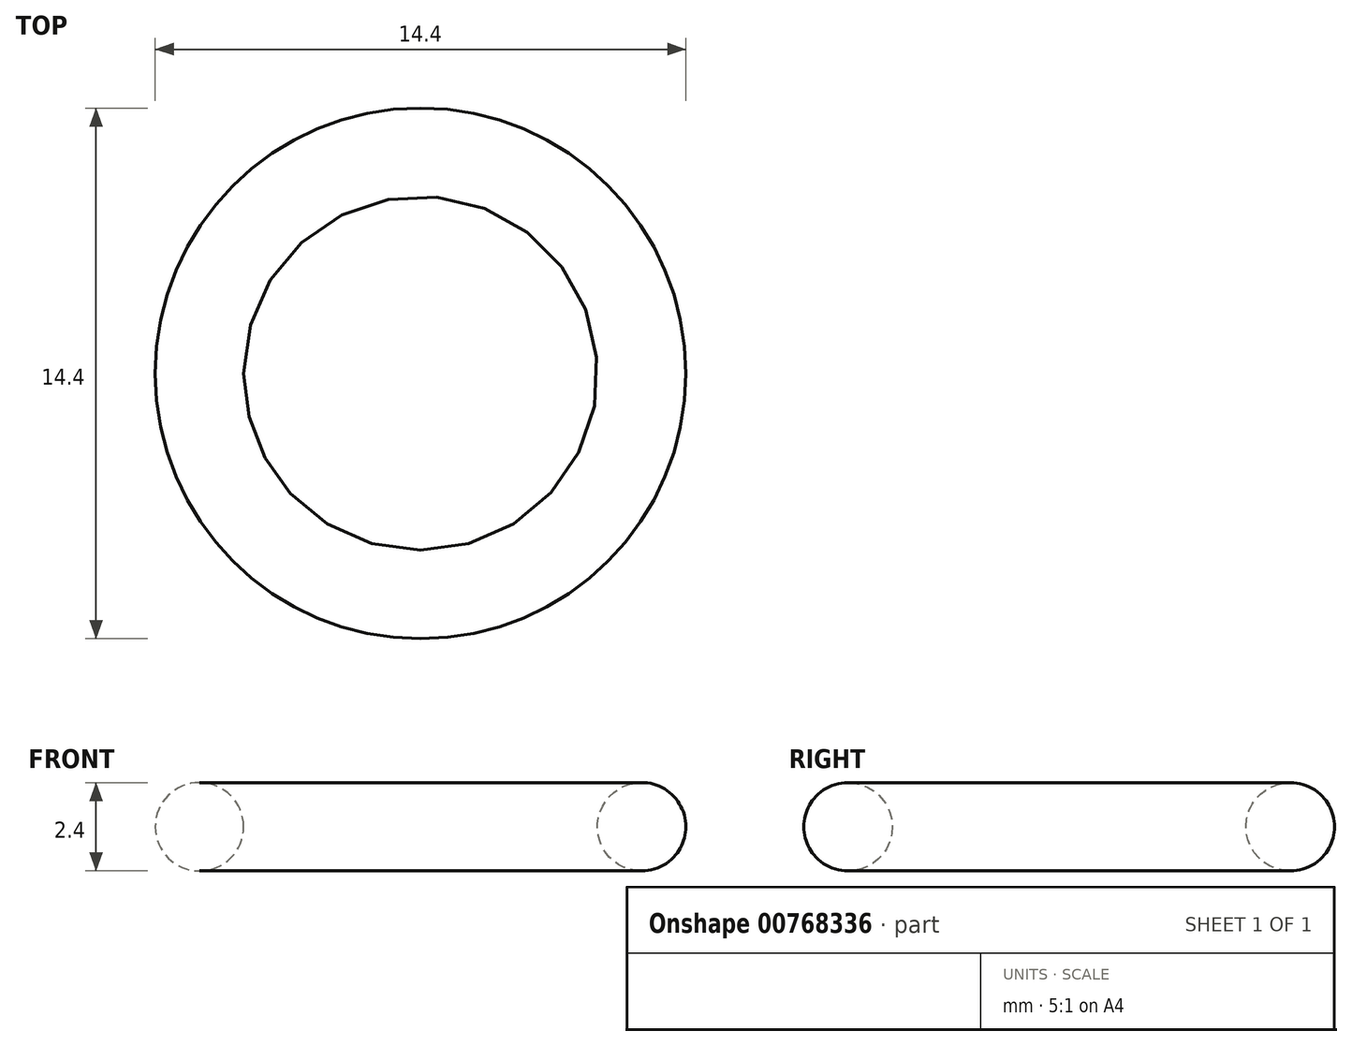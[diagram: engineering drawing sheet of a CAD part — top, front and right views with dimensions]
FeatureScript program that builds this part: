
annotation { "Feature Type Name" : "Feature", "Feature Type Description" : "" }
export const myFeature = defineFeature(function(context is Context, id is Id, definition is map)
    precondition{}
    {
        {
            var Q0;
            Q0=qCreatedBy(makeId("Front.planeOp"),FACE);
            var sketch = newSketch(context, id + "F0", { "sketchPlane" : qUnion([Q0])});
            skCircle(sketch, "E0", {"center": v(-6, 0) * mm, "radius": 1.2 * mm});
            skSolve(sketch);
        }
        {
            var Q0;
            Q0=qCreatedBy(makeId("Front.planeOp"),FACE);
            var sketch = newSketch(context, id + "F1", { "sketchPlane" : qUnion([Q0])});
            skLineSegment(sketch, "E1", {"start": v(0, -4.35) * mm, "end": v(0, 5.64) * mm});
            skSolve(sketch);
        }
        {
            var Q0;
            Q0=makeQuery(id+"F0.imprint","IMPRINT",FACE,{"disambiguationData":[TD([[makeQuery(id+"F0.imprint","IMPRINT",EDGE,{"derivedFrom":sQuery(id+"F0.wireOp",EDGE,"E0")}),1.0]])]});
            var Q1;
            Q1=sQuery(id+"F1.wireOp",EDGE,"E1");
            revolve(context, id + "F2", {"surfaceOperationType" : NewSurfaceOperationType.NEW, "entities" : qUnion([Q0]), "axis" : qUnion([Q1]), "revolveType" : RevolveType.FULL});
        }
    });
